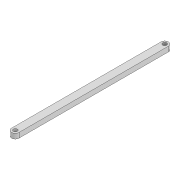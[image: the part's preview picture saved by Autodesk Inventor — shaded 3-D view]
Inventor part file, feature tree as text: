
AUTODESK INVENTOR PART (.ipt)
format: ipt  version: 2022 (Build 260153000, 153)  size: 86,528 bytes
history: native  units: mm
features: extrude x1, sketch x1
ambient origin geometry x8: Origin, YZ Plane, XZ Plane, XY Plane, X Axis, Y Axis, Z Axis, Center Point
bodies: Solid1 (feature_tree)
feature tree (2):
  extrude  "Extrusion1"  Depth=4.0mm
  sketch  "Sketch1"  dims[d0=3.2mm d1=3.2mm d2=6.0mm d3=120.294mm d6=4.0mm d7=0.0mm]
